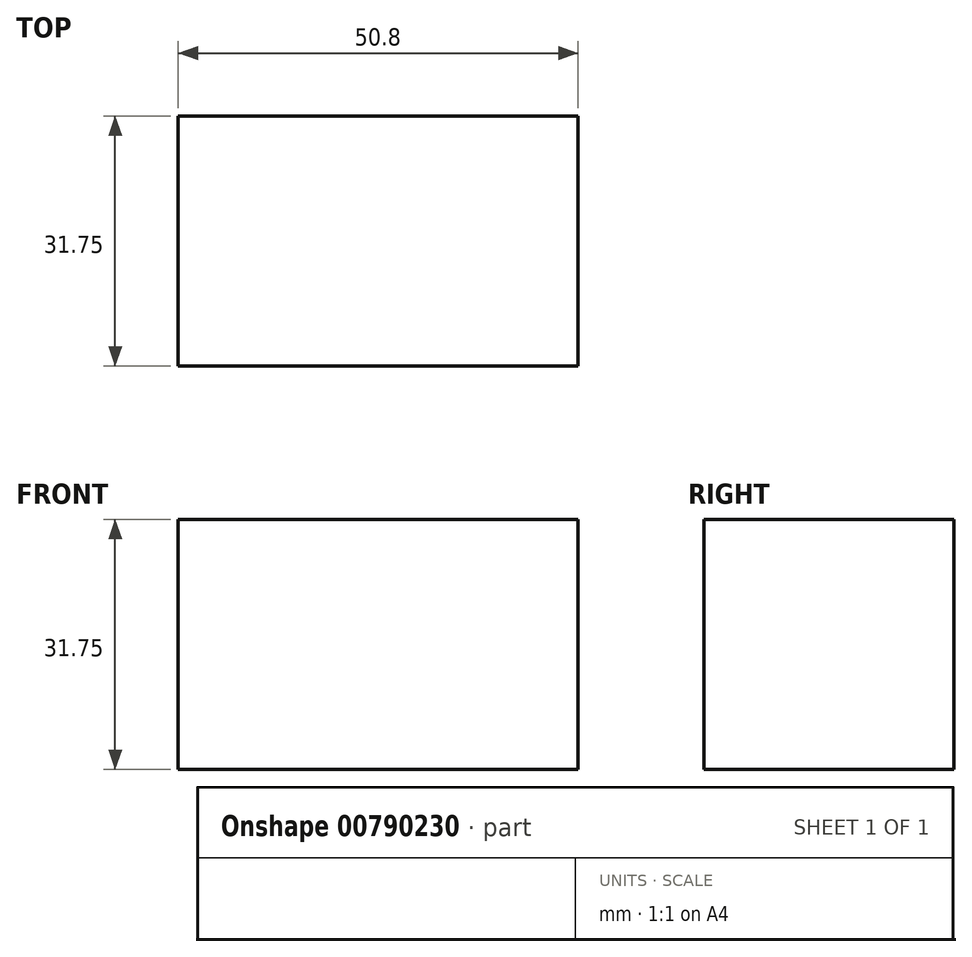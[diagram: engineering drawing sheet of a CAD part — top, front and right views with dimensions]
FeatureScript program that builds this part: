
annotation { "Feature Type Name" : "Feature", "Feature Type Description" : "" }
export const myFeature = defineFeature(function(context is Context, id is Id, definition is map)
    precondition{}
    {
        {
            var Q0;
            Q0=qCreatedBy(makeId("Front.planeOp"),FACE);
            var sketch = newSketch(context, id + "F0", { "sketchPlane" : qUnion([Q0])});
            skLineSegment(sketch, "E0", {"start": v(0, 0) * mm, "end": v(50.8, 0) * mm});
            skLineSegment(sketch, "E1", {"start": v(50.8, 0) * mm, "end": v(50.8, 31.75) * mm});
            skLineSegment(sketch, "E2", {"start": v(50.8, 31.75) * mm, "end": v(0, 31.75) * mm});
            skLineSegment(sketch, "E3", {"start": v(0, 31.75) * mm, "end": v(0, 0) * mm});
            skSolve(sketch);
        }
        {
            var Q0;
            Q0=makeQuery(id+"F0.imprint","IMPRINT",FACE,{"disambiguationData":[TD([[makeQuery(id+"F0.imprint","IMPRINT",EDGE,{"derivedFrom":sQuery(id+"F0.wireOp",EDGE,"E0")}),1.0]])]});
            extrude(context, id + "F1", {"entities" : qUnion([Q0]), "depth" : 31.75 * mm, "offsetDistance" : 25.4 * mm});
        }
    });
